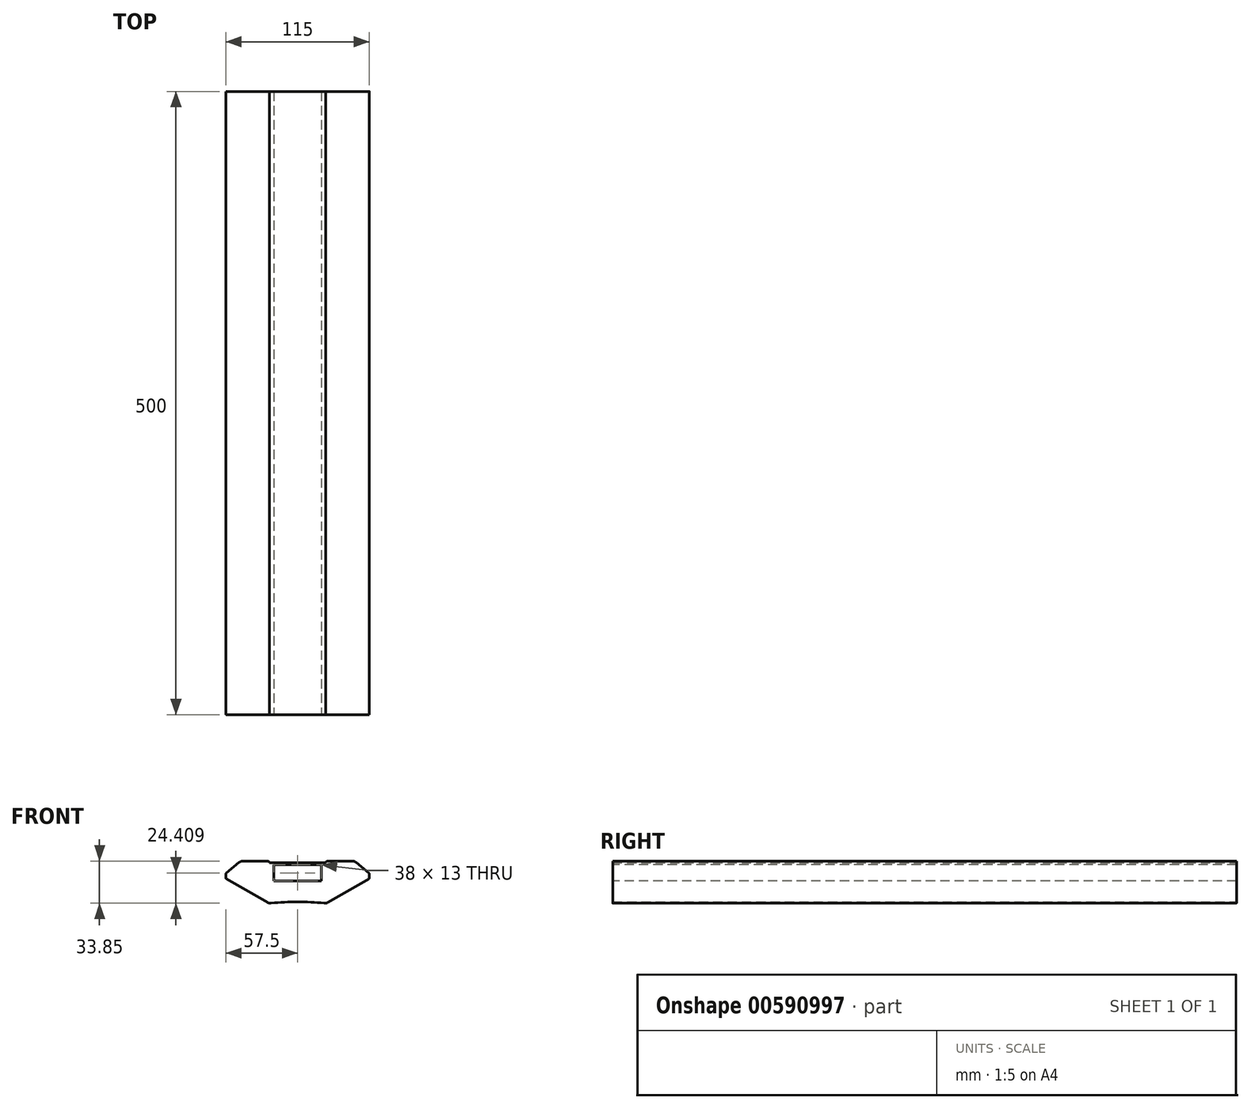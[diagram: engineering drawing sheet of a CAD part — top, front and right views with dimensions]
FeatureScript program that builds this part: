
annotation { "Feature Type Name" : "Feature", "Feature Type Description" : "" }
export const myFeature = defineFeature(function(context is Context, id is Id, definition is map)
    precondition{}
    {
        {
            var Q0;
            Q0=qCreatedBy(makeId("Front.planeOp"),FACE);
            var sketch = newSketch(context, id + "F0", { "sketchPlane" : qUnion([Q0])});
            skLineSegment(sketch, "E0", {"start": v(0, 0) * mm, "end": v(0, 59.48) * mm, "construction": true});
            skLineSegment(sketch, "E1", {"start": v(0, 29.74) * mm, "end": v(22.5, 29.74) * mm});
            skLineSegment(sketch, "E2", {"start": v(22.5, 29.74) * mm, "end": v(22.5, 31.04) * mm});
            skLineSegment(sketch, "E3", {"start": v(22.5, 31.04) * mm, "end": v(45.58, 31.04) * mm});
            skLineSegment(sketch, "E4", {"start": v(45.58, 31.04) * mm, "end": v(57.5, 21.04) * mm});
            skLineSegment(sketch, "E5", {"start": v(57.5, 21.04) * mm, "end": v(57.5, 17.04) * mm});
            skLineSegment(sketch, "E6", {"start": v(57.5, 17.04) * mm, "end": v(22.86, -2.96) * mm});
            skLineSegment(sketch, "E7.MirrorCS", {"start": v(0, 29.74) * mm, "end": v(-22.5, 29.74) * mm});
            skLineSegment(sketch, "E8.MirrorCS", {"start": v(-22.5, 29.74) * mm, "end": v(-22.5, 31.04) * mm});
            skLineSegment(sketch, "E9.MirrorCS", {"start": v(-22.5, 31.04) * mm, "end": v(-45.58, 31.04) * mm});
            skLineSegment(sketch, "E10.MirrorCS", {"start": v(-45.58, 31.04) * mm, "end": v(-57.5, 21.04) * mm});
            skLineSegment(sketch, "E11.MirrorCS", {"start": v(-57.5, 21.04) * mm, "end": v(-57.5, 17.04) * mm});
            skLineSegment(sketch, "E12.MirrorCS", {"start": v(-57.5, 17.04) * mm, "end": v(-22.86, -2.96) * mm});
            skArc(sketch, "E13", {"start": v(22.86, -2.96) * mm, "mid": v(0, -1.65) * mm, "end": v(-22.86, -2.96) * mm});
            skLineSegment(sketch, "E14", {"start": v(-64.98, 21.36) * mm, "end": v(-64.98, -33.36) * mm});
            skLineSegment(sketch, "E15", {"start": v(826.7, 31.04) * mm, "end": v(972.31, 29.74) * mm});
            skPoint(sketch, "E15.endSnap0", {"position": v(11.25, 29.74) * mm});
            skSolve(sketch);
        }
        {
            var Q0;
            Q0 = qSketchRegion(id + "F0", true);
            extrude(context, id + "F1", {"entities" : qUnion([Q0]), "endBound" : BoundingType.SYMMETRIC, "depth" : 500 * mm, "offsetDistance" : 25 * mm});
        }
        {
            var Q0;
            Q0=makeQuery(id+"F1.opExtrude","SWEPT_EDGE",EDGE,{"disambiguationData":[OSD([sQuery(id+"F0.wireOp",EDGE,"E3"),sQuery(id+"F0.wireOp",EDGE,"E4")])]});
            var Q1;
            Q1=makeQuery(id+"F1.opExtrude","SWEPT_EDGE",EDGE,{"disambiguationData":[OSD([sQuery(id+"F0.wireOp",EDGE,"E6"),sQuery(id+"F0.wireOp",EDGE,"E13")])]});
            var Q2;
            Q2=makeQuery(id+"F1.opExtrude","SWEPT_EDGE",EDGE,{"disambiguationData":[OSD([sQuery(id+"F0.wireOp",EDGE,"E9.MirrorCS"),sQuery(id+"F0.wireOp",EDGE,"E10.MirrorCS")])]});
            var Q3;
            Q3=makeQuery(id+"F1.opExtrude","SWEPT_EDGE",EDGE,{"disambiguationData":[OSD([sQuery(id+"F0.wireOp",EDGE,"E12.MirrorCS"),sQuery(id+"F0.wireOp",EDGE,"E13")])]});
            fillet(context, id + "F2", {"entities" : qUnion([Q0, Q1, Q2, Q3]), "radius" : 5 * mm, "tangentPropagation" : true, "allowEdgeOverflow" : false});
        }
        {
            var Q0;
            Q0=makeQuery(id+"F1.opExtrude","SWEPT_EDGE",EDGE,{"disambiguationData":[OSD([sQuery(id+"F0.wireOp",EDGE,"E4"),sQuery(id+"F0.wireOp",EDGE,"E5")])]});
            var Q1;
            Q1=makeQuery(id+"F1.opExtrude","SWEPT_EDGE",EDGE,{"disambiguationData":[OSD([sQuery(id+"F0.wireOp",EDGE,"E5"),sQuery(id+"F0.wireOp",EDGE,"E6")])]});
            var Q2;
            Q2=makeQuery(id+"F1.opExtrude","SWEPT_EDGE",EDGE,{"disambiguationData":[OSD([sQuery(id+"F0.wireOp",EDGE,"E10.MirrorCS"),sQuery(id+"F0.wireOp",EDGE,"E11.MirrorCS")])]});
            var Q3;
            Q3=makeQuery(id+"F1.opExtrude","SWEPT_EDGE",EDGE,{"disambiguationData":[OSD([sQuery(id+"F0.wireOp",EDGE,"E11.MirrorCS"),sQuery(id+"F0.wireOp",EDGE,"E12.MirrorCS")])]});
            fillet(context, id + "F3", {"entities" : qUnion([Q0, Q1, Q2, Q3]), "radius" : 1 * mm, "tangentPropagation" : true, "allowEdgeOverflow" : false});
        }
        {
            var Q0;
            Q0=makeQuery(id+"F1.opExtrude","CAP_FACE",FACE,{"disambiguationData":[OSD([sQuery(id+"F0.wireOp",EDGE,"E1"),sQuery(id+"F0.wireOp",EDGE,"E2"),sQuery(id+"F0.wireOp",EDGE,"E3"),sQuery(id+"F0.wireOp",EDGE,"E4"),sQuery(id+"F0.wireOp",EDGE,"E5"),sQuery(id+"F0.wireOp",EDGE,"E6"),sQuery(id+"F0.wireOp",EDGE,"E7.MirrorCS"),sQuery(id+"F0.wireOp",EDGE,"E8.MirrorCS"),sQuery(id+"F0.wireOp",EDGE,"E9.MirrorCS"),sQuery(id+"F0.wireOp",EDGE,"E10.MirrorCS"),sQuery(id+"F0.wireOp",EDGE,"E11.MirrorCS"),sQuery(id+"F0.wireOp",EDGE,"E12.MirrorCS"),sQuery(id+"F0.wireOp",EDGE,"E13")])],"isStart":false});
            var sketch = newSketch(context, id + "F4", { "sketchPlane" : qUnion([Q0])});
            skLineSegment(sketch, "E16.bottom", {"start": v(-19, 28.1) * mm, "end": v(19, 28.1) * mm});
            skLineSegment(sketch, "E16.top", {"start": v(-19, 15.1) * mm, "end": v(19, 15.1) * mm});
            skLineSegment(sketch, "E16.left", {"start": v(-19, 28.1) * mm, "end": v(-19, 15.1) * mm});
            skLineSegment(sketch, "E16.right", {"start": v(19, 28.1) * mm, "end": v(19, 15.1) * mm});
            skSolve(sketch);
        }
        {
            var Q0;
            Q0=makeQuery(id+"F4.imprint","IMPRINT",FACE,{"disambiguationData":[TD([[makeQuery(id+"F4.imprint","IMPRINT",EDGE,{"derivedFrom":sQuery(id+"F4.wireOp",EDGE,"E16.bottom")}),-1.0]])]});
            extrude(context, id + "F5", {"entities" : qUnion([Q0]), "operationType" : NewBodyOperationType.REMOVE, "endBound" : BoundingType.THROUGH_ALL, "oppositeDirection" : true, "depth" : 500 * mm, "offsetDistance" : 25 * mm});
        }
        {
            var Q0;
            Q0=makeQuery(id+"F1.opExtrude","SWEPT_EDGE",EDGE,{"disambiguationData":[OSD([sQuery(id+"F0.wireOp",EDGE,"E8.MirrorCS"),sQuery(id+"F0.wireOp",EDGE,"E9.MirrorCS")])]});
            var Q1;
            Q1=makeQuery(id+"F1.opExtrude","SWEPT_EDGE",EDGE,{"disambiguationData":[OSD([sQuery(id+"F0.wireOp",EDGE,"E2"),sQuery(id+"F0.wireOp",EDGE,"E3")])]});
            fillet(context, id + "F6", {"entities" : qUnion([Q0, Q1]), "radius" : 2 * mm, "tangentPropagation" : true, "allowEdgeOverflow" : false});
        }
    });
